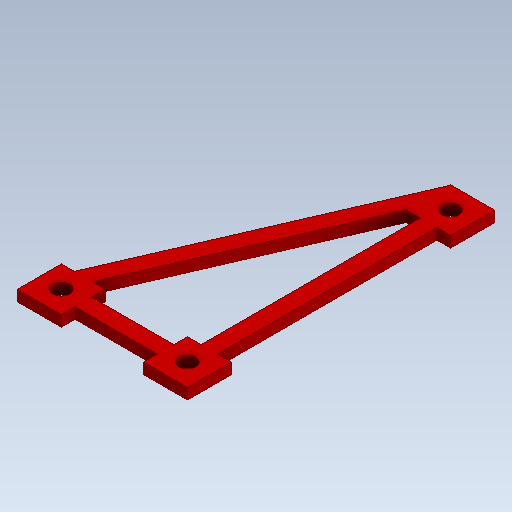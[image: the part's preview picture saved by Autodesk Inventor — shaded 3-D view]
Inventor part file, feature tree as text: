
AUTODESK INVENTOR PART (.ipt)
format: ipt  version: 2020 (Build 240168000, 168)  size: 159,744 bytes
history: native  units: mm
features: sketch x2, other x1, extrude x1
ambient origin geometry x8: Origin, YZ Plane, XZ Plane, XY Plane, X Axis, Y Axis, Z Axis, Center Point
bodies: Solid1 (feature_tree)
feature tree (4):
  other  "HexBodyV2.ipt"
  extrude  "Extrusion1"  Depth=10.0mm
  sketch  "Sketch14"  dims[d2=3.1mm d3=3.1mm d4=3.0mm d5=3.0mm d6=3.0mm d7=2.0mm d8=0.0mm]
  sketch  "Sketch2"  dims[d0=10.0mm d1=3.1mm]
